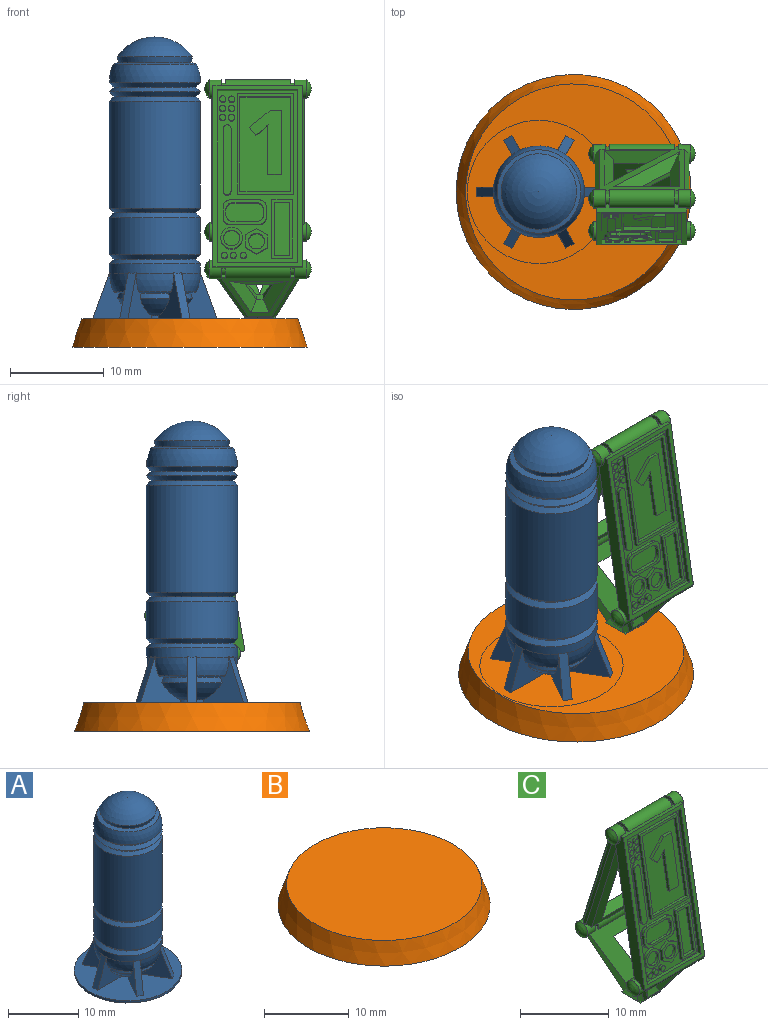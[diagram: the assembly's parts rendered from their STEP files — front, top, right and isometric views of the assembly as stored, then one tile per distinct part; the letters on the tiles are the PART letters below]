
ASSEMBLY  parts=3 mates=2
PART A: 66 faces, bbox 15.5x15.5x30.6 mm
  f0: cylinder r=4.85mm len=9.7mm, axis (0,0,-1), area 30.3mm2, adj f3,f8,f13,f18,f22,f28,f29,f48
  f1: plane 15.25x15.25mm, normal (0,0,1), area 143.6mm2, adj f2,f7,f12,f17,f26,f33,f34,f48
  f2: cylinder r=1.76mm len=0.71mm, axis (0,0,-1), area 0.3mm2, adj f1,f32,f49,f63
  f3: sphere r=4.85mm, area 7.9mm2, adj f0,f4,f60,f64
  f4: cone r=4.44mm half-angle=74deg, axis (0,0,1), area 2.1mm2, adj f3,f5,f60,f64
  f5: cone r=3.84mm half-angle=16deg, axis (0,0,-1), area 1.9mm2, adj f4,f6,f60,f64
  f6: sphere r=4.85mm, area 5.7mm2, adj f5,f7,f60,f64
  f7: cylinder r=1.76mm len=0.82mm, axis (0,0,-1), area 0.3mm2, adj f1,f6,f60,f64
  f8: sphere r=4.85mm, area 7.9mm2, adj f0,f9,f57,f61
  f9: cone r=4.44mm half-angle=74deg, axis (0,0,1), area 2.1mm2, adj f8,f10,f57,f61
  f10: cone r=3.84mm half-angle=16deg, axis (0,0,-1), area 1.9mm2, adj f9,f11,f57,f61
  f11: sphere r=4.85mm, area 5.7mm2, adj f10,f12,f57,f61
  f12: cylinder r=1.76mm len=0.71mm, axis (0,0,-1), area 0.3mm2, adj f1,f11,f57,f61
  f13: sphere r=4.85mm, area 7.9mm2, adj f0,f14,f54,f58
  f14: cone r=4.44mm half-angle=74deg, axis (0,0,1), area 2.1mm2, adj f13,f15,f54,f58
  f15: cone r=3.84mm half-angle=16deg, axis (0,0,-1), area 1.9mm2, adj f14,f16,f54,f58
  f16: sphere r=4.85mm, area 5.7mm2, adj f15,f17,f54,f58
  f17: cylinder r=1.76mm len=0.71mm, axis (0,0,-1), area 0.3mm2, adj f1,f16,f54,f58
  f18: sphere r=4.85mm, area 7.9mm2, adj f0,f19,f51,f55
  f19: cone r=4.44mm half-angle=74deg, axis (0,0,1), area 2.1mm2, adj f18,f20,f51,f55
  f20: cone r=3.84mm half-angle=16deg, axis (0,0,-1), area 1.9mm2, adj f19,f21,f51,f55
  f21: sphere r=4.85mm, area 5.7mm2, adj f20,f26,f51,f55
  f22: sphere r=4.85mm, area 7.9mm2, adj f0,f23,f48,f52
  f23: cone r=4.44mm half-angle=74deg, axis (0,0,1), area 2.1mm2, adj f22,f24,f48,f52
  f24: cone r=3.84mm half-angle=16deg, axis (0,0,-1), area 1.9mm2, adj f23,f25,f48,f52
  f25: sphere r=4.85mm, area 5.7mm2, adj f24,f33,f48,f52
  f26: cylinder r=1.76mm len=0.82mm, axis (0,0,-1), area 0.3mm2, adj f1,f21,f51,f55
  f27: cone r=4.85mm half-angle=45deg, axis (0,0,1), area 20.3mm2, adj f28,f47
  f28: cone r=4.35mm half-angle=45deg, axis (0,0,-1), area 20.3mm2, adj f0,f27
  f29: sphere r=4.85mm, area 7.9mm2, adj f0,f30,f49,f63
  f30: cone r=4.44mm half-angle=74deg, axis (0,0,1), area 2.1mm2, adj f29,f31,f49,f63
  f31: cone r=3.84mm half-angle=16deg, axis (0,0,-1), area 1.9mm2, adj f30,f32,f49,f63
  f32: sphere r=4.85mm, area 5.7mm2, adj f2,f31,f49,f63
  f33: cylinder r=1.76mm len=0.71mm, axis (0,0,-1), area 0.3mm2, adj f1,f25,f48,f52
  f34: cylinder r=7.62mm len=15.25mm, axis (0,0,-1), area 18.3mm2, adj f1,f35
  f35: plane 15.25x15.25mm, normal (0,0,-1), area 182.6mm2, adj f34
  f36: sphere r=4.85mm, area 64.8mm2, adj f37
  f37: cone r=3.84mm half-angle=16deg, axis (0,0,1), area 15.3mm2, adj f36,f38
  f38: cone r=4.44mm half-angle=74deg, axis (0,0,-1), area 16.1mm2, adj f37,f39
  f39: sphere r=4.85mm, area 59.6mm2, adj f38,f40
  f40: cone r=4.85mm half-angle=45deg, axis (0,0,1), area 20.4mm2, adj f39,f41
  f41: cone r=4.35mm half-angle=45deg, axis (0,0,-1), area 20.4mm2, adj f40,f42
  f42: cone r=4.35mm half-angle=45deg, axis (0,0,1), area 20.3mm2, adj f41,f43
  f43: cone r=4.85mm half-angle=45deg, axis (0,0,-1), area 20.3mm2, adj f42,f44
  f44: cylinder r=4.85mm len=11.39mm, axis (0,0,-1), area 346.9mm2, adj f43,f45
  f45: cone r=4.85mm half-angle=46.1deg, axis (0,0,1), area 20mm2, adj f44,f46
  f46: cone r=4.35mm half-angle=43.9deg, axis (0,0,-1), area 20.8mm2, adj f45,f47
  f47: cylinder r=4.85mm len=9.7mm, axis (0,0,-1), area 119.8mm2, adj f27,f46
  f48: plane 5.17x5.16mm, normal (0,-1,0), area 9.5mm2, adj f0,f1,f22,f23,f24,f25,f33,f50
  f49: plane 5.17x5.16mm, normal (0,1,0), area 9.5mm2, adj f0,f1,f2,f29,f30,f31,f32,f50
  f50: plane 4.96x1.83mm, normal (-0.94,0,0.34), area 5.2mm2, adj f0,f1,f48,f49
  f51: plane 5.16x4.51mm, normal (0.87,-0.5,0), area 9.5mm2, adj f0,f1,f18,f19,f20,f21,f26,f53
  f52: plane 5.16x4.51mm, normal (-0.87,0.5,0), area 9.5mm2, adj f0,f1,f22,f23,f24,f25,f33,f53
  f53: plane 4.92x2.05mm, normal (-0.47,-0.81,0.34), area 5.2mm2, adj f0,f1,f51,f52
  f54: plane 5.16x4.51mm, normal (0.87,0.5,0), area 9.5mm2, adj f0,f1,f13,f14,f15,f16,f17,f56
  f55: plane 5.16x4.51mm, normal (-0.87,-0.5,0), area 9.5mm2, adj f0,f1,f18,f19,f20,f21,f26,f56
  f56: plane 4.92x2.05mm, normal (0.47,-0.81,0.34), area 5.2mm2, adj f0,f1,f54,f55
  f57: plane 5.17x5.16mm, normal (0,1,0), area 9.5mm2, adj f0,f1,f8,f9,f10,f11,f12,f59
  f58: plane 5.17x5.16mm, normal (0,-1,0), area 9.5mm2, adj f0,f1,f13,f14,f15,f16,f17,f59
  f59: plane 4.92x1.79mm, normal (0.94,0,0.34), area 5.2mm2, adj f0,f1,f57,f58
  f60: plane 5.16x4.51mm, normal (-0.87,0.5,0), area 9.5mm2, adj f0,f1,f3,f4,f5,f6,f7,f62
  f61: plane 5.16x4.51mm, normal (0.87,-0.5,0), area 9.5mm2, adj f0,f1,f8,f9,f10,f11,f12,f62
  f62: plane 4.92x2.05mm, normal (0.47,0.81,0.34), area 5.2mm2, adj f0,f1,f60,f61
  f63: plane 5.16x4.51mm, normal (-0.87,-0.5,0), area 9.5mm2, adj f0,f1,f2,f29,f30,f31,f32,f65
  f64: plane 5.16x4.51mm, normal (0.87,0.5,0), area 9.5mm2, adj f0,f1,f3,f4,f5,f6,f7,f65
  f65: plane 4.92x2.05mm, normal (-0.47,0.81,0.34), area 5.2mm2, adj f0,f1,f63,f64
PART B: 5 faces, bbox 25x25x3 mm
  f0: plane 25x25mm, normal (0,0,-1), area 483.3mm2, adj f2,f3
  f1: plane 23x23mm, normal (0,0,1), area 415.5mm2, adj f2
  f2: cone r=12.5mm half-angle=18.4deg, axis (0,0,-1), area 238.4mm2, adj f0,f1
  f3: cylinder r=1.55mm len=3.1mm, axis (0,0,-1), area 22.4mm2, adj f0,f4
  f4: plane 3.1x3.1mm, normal (0,0,-1), area 7.5mm2, adj f3
PART C: 207 faces, bbox 11.4x10.7x25.5 mm
  f0: plane 0.4x0.15mm, normal (0,0,1), area 0.1mm2, adj f2,f25,f26,f30
  f1: plane 7.81x4.18mm, normal (0,-0.84,-0.54), area 8.5mm2, adj f4,f5,f9,f10,f11,f16,f17,f18
  f2: plane 9.66x5.27mm, normal (0,0.73,0.68), area 30.6mm2, adj f0,f3,f6,f7,f8,f12,f13,f14
  f3: plane 5.37x5.03mm, normal (-0.82,0,-0.57), area 10.8mm2, adj f2,f5,f6,f35
  f4: plane 0.4x0.25mm, normal (0,-0.88,0.48), area 0.1mm2, adj f1,f36,f37,f38
  f5: plane 4.35x3.29mm, normal (-0.51,-0.52,-0.69), area 3.6mm2, adj f1,f3,f11,f20,f22,f35,f36
  f6: plane 3.1x3.04mm, normal (0,0,-1), area 9.4mm2, adj f2,f3,f8,f20,f21,f22
  f7: plane 0.4x0.15mm, normal (0,0,1), area 0.1mm2, adj f2,f27,f28,f29
  f8: plane 5.35x5.03mm, normal (0.85,0,-0.52), area 10.3mm2, adj f2,f6,f10,f34
  f9: plane 0.4x0.25mm, normal (0,-0.88,0.48), area 0.1mm2, adj f1,f40,f41,f42
  f10: plane 4.32x3.22mm, normal (0.53,-0.53,-0.66), area 3.6mm2, adj f1,f8,f11,f20,f21,f34
  f11: plane 2.64x0.23mm, normal (0,-0.48,-0.88), area 0.7mm2, adj f1,f5,f10,f20
  f12: plane 0.78x0.73mm, normal (0,-0.54,0.84), area 0.7mm2, adj f2,f13,f14,f19
  f13: plane 1.96x1.84mm, normal (0.86,-0.27,0.42), area 1.7mm2, adj f2,f12,f15,f17
  f14: plane 1.96x1.84mm, normal (-0.89,-0.25,0.38), area 1.7mm2, adj f2,f12,f15,f18
  f15: plane 2.89x0.48mm, normal (0,0.54,-0.84), area 1.6mm2, adj f2,f13,f14,f16
  f16: plane 6.27x1.38mm, normal (0,-0.21,-0.98), area 6.5mm2, adj f1,f15,f17,f18
  f17: plane 3.34x2.89mm, normal (0.61,-0.79,-0.08), area 4.9mm2, adj f1,f13,f16,f19
  f18: plane 3.34x2.64mm, normal (-0.63,-0.77,-0.11), area 4.7mm2, adj f1,f14,f16,f19
  f19: plane 1.92x1.38mm, normal (0,-0.98,0.21), area 1.9mm2, adj f1,f12,f17,f18
  f20: plane 3.33x0.33mm, normal (0,-0.89,0.46), area 0.5mm2, adj f5,f6,f10,f11,f21,f22
  f21: plane 0.47x0.33mm, normal (0.95,0,-0.33), area 0.1mm2, adj f6,f10,f20
  f22: plane 0.45x0.31mm, normal (-0.93,0,-0.37), area 0.1mm2, adj f5,f6,f20
  f23: cylinder r=1mm len=6.97mm, axis (1,0,0), area 11.4mm2, adj f1,f38,f40,f115
  f24: plane 1.1x0.37mm, normal (0,0.58,-0.82), area 0.4mm2, adj f2,f48,f49,f55
  f25: cylinder r=0.6mm len=0.59mm, axis (1,0,0), area 0.3mm2, adj f0,f26,f30,f116
  f26: plane 1.22x0.9mm, normal (-1,0,0), area 0.5mm2, adj f0,f2,f25,f39,f116
  f27: plane 1.22x0.9mm, normal (1,0,0), area 0.5mm2, adj f2,f7,f28,f39,f116
  f28: cylinder r=0.6mm len=0.59mm, axis (1,0,0), area 0.3mm2, adj f7,f27,f29,f116
  f29: plane 1.22x0.9mm, normal (-1,0,0), area 0.5mm2, adj f2,f7,f28,f34,f116
  f30: plane 1.22x0.9mm, normal (1,0,0), area 0.5mm2, adj f0,f2,f25,f35,f116
  f31: plane 8.42x4.24mm, normal (-0.93,0,-0.37), area 12.3mm2, adj f2,f33,f50,f70
  f32: plane 8.41x4.23mm, normal (0.95,0,-0.33), area 12mm2, adj f2,f33,f49,f67
  f33: plane 9.72x7.18mm, normal (0,-0.89,0.46), area 45.6mm2, adj f2,f31,f32,f45,f47,f52,f53,f54
  f34: cylinder r=1mm len=2mm, axis (1,0,0), area 6mm2, adj f1,f2,f8,f10,f29,f42,f43,f112
  f35: cylinder r=1mm len=2mm, axis (1,0,0), area 6.1mm2, adj f2,f3,f5,f30,f36,f44,f114,f115
  f36: plane 1.17x0.95mm, normal (1,0,0), area 0.5mm2, adj f1,f4,f5,f35,f37,f115
  f37: cylinder r=0.6mm len=0.7mm, axis (1,0,0), area 0.4mm2, adj f4,f36,f38,f115
  f38: plane 1.17x0.93mm, normal (-1,0,0), area 0.5mm2, adj f1,f4,f23,f37,f115
  f39: cylinder r=1mm len=6.97mm, axis (1,0,0), area 11.4mm2, adj f2,f26,f27,f116
  f40: plane 1.17x0.93mm, normal (1,0,0), area 0.5mm2, adj f1,f9,f23,f41,f115
  f41: cylinder r=0.6mm len=0.7mm, axis (1,0,0), area 0.4mm2, adj f9,f40,f42,f115
  f42: plane 1.17x0.93mm, normal (-1,0,0), area 0.5mm2, adj f1,f9,f34,f41,f115
  f43: revolved ~2x2mm, area 3.8mm2, adj f34
  f44: revolved ~2x2mm, area 3.8mm2, adj f35
  f45: plane 0.4x0.16mm, normal (0,0,1), area 0.1mm2, adj f33,f58,f60,f61
  f46: plane 8.03x0.37mm, normal (0,0.82,0.58), area 0.6mm2, adj f48,f49,f50,f65,f66,f67,f70,f71
  f47: plane 0.4x0.16mm, normal (0,0,1), area 0.1mm2, adj f33,f59,f63,f64
  f48: plane 7.94x7.85mm, normal (0,0.94,-0.33), area 12.2mm2, adj f24,f46,f49,f50,f51,f55,f56,f57
  f49: plane 8.15x3.45mm, normal (0.63,0.63,-0.44), area 8.3mm2, adj f2,f24,f32,f46,f48,f67
  f50: plane 8.15x3.77mm, normal (-0.62,0.63,-0.47), area 8.4mm2, adj f2,f31,f46,f48,f51,f70
  f51: plane 1.12x0.37mm, normal (0,0.58,-0.82), area 0.4mm2, adj f2,f48,f50,f57
  f52: plane 5.25x3.14mm, normal (-0.95,0.1,0.29), area 6mm2, adj f33,f53,f54,f55
  f53: plane 5.25x3.14mm, normal (0.94,0.12,0.33), area 6.1mm2, adj f33,f52,f54,f57
  f54: plane 3.71x0.67mm, normal (0,-0.33,-0.94), area 2.7mm2, adj f33,f52,f53,f56
  f55: plane 7.64x3.11mm, normal (-0.67,0.74,-0.03), area 10.5mm2, adj f2,f24,f48,f52,f56,f57
  f56: plane 6.53x1.28mm, normal (0,0.43,-0.9), area 7.2mm2, adj f48,f54,f55,f57
  f57: plane 7.64x3.46mm, normal (0.66,0.75,0), area 10.7mm2, adj f2,f48,f51,f53,f55,f56
  f58: cylinder r=0.6mm len=0.4mm, axis (1,0,0), area 0.1mm2, adj f45,f60,f61,f79
  f59: cylinder r=0.6mm len=0.4mm, axis (1,0,0), area 0.1mm2, adj f47,f63,f64,f87
  f60: plane 0.78x0.42mm, normal (1,0,0), area 0.2mm2, adj f33,f45,f58,f70,f77,f79
  f61: plane 0.78x0.42mm, normal (-1,0,0), area 0.2mm2, adj f33,f45,f58,f62,f77,f79
  f62: cylinder r=1mm len=6.97mm, axis (1,0,0), area 5.6mm2, adj f33,f61,f63,f77
  f63: plane 0.78x0.42mm, normal (1,0,0), area 0.2mm2, adj f33,f47,f59,f62,f77,f87
  f64: plane 0.78x0.42mm, normal (-1,0,0), area 0.2mm2, adj f33,f47,f59,f67,f77,f87
  f65: cylinder r=0.6mm len=0.57mm, axis (1,0,0), area 0.3mm2, adj f46,f71,f72,f78
  f66: cylinder r=0.6mm len=0.57mm, axis (1,0,0), area 0.3mm2, adj f46,f74,f75,f83
  f67: cylinder r=1mm len=2mm, axis (1,0,0), area 5.6mm2, adj f32,f33,f46,f49,f64,f68,f75,f76
  f68: revolved ~2x2mm, area 3.8mm2, adj f67
  f69: revolved ~2x2mm, area 3.8mm2, adj f70
  f70: cylinder r=1mm len=2mm, axis (1,0,0), area 5.7mm2, adj f31,f33,f46,f50,f60,f69,f71,f76
  f71: plane 1.78x0.82mm, normal (1,0,0), area 0.6mm2, adj f46,f65,f70,f76,f78
  f72: plane 1.78x0.82mm, normal (-1,0,0), area 0.6mm2, adj f46,f65,f73,f76,f78
  f73: cylinder r=1mm len=6.97mm, axis (1,0,0), area 15.3mm2, adj f46,f72,f74,f76
  f74: plane 1.78x0.82mm, normal (1,0,0), area 0.6mm2, adj f46,f66,f73,f76,f83
  f75: plane 1.78x0.82mm, normal (-1,0,0), area 0.6mm2, adj f46,f66,f67,f76,f83
  f76: plane 15.2x8.97mm, normal (0,0.95,0.3), area 44.3mm2, adj f67,f70,f71,f72,f73,f74,f75,f78
  f77: plane 13.5x8.97mm, normal (0,-0.96,-0.3), area 83.3mm2, adj f60,f61,f62,f63,f64,f67,f70,f79
  f78: plane 0.4x0.17mm, normal (0,0,-1), area 0.1mm2, adj f65,f71,f72,f76
  f79: plane 0.4x0.29mm, normal (0,-0.59,-0.8), area 0.1mm2, adj f58,f60,f61,f77
  f80: plane 0.4x0.24mm, normal (0,0,1), area 0.1mm2, adj f76,f104,f105,f106
  f81: plane 13.78x4.55mm, normal (-0.71,-0.68,-0.21), area 10mm2, adj f70,f77,f84,f103,f116
  f82: plane 0.4x0.24mm, normal (0,0,1), area 0.1mm2, adj f76,f108,f109,f110
  f83: plane 0.4x0.17mm, normal (0,0,-1), area 0.1mm2, adj f66,f74,f75,f76
  f84: plane 13.52x4.58mm, normal (-1,0,0), area 6.3mm2, adj f70,f81,f88,f103
  f85: plane 13.52x4.58mm, normal (1,0,0), area 6.3mm2, adj f67,f86,f89,f100
  f86: plane 13.78x4.55mm, normal (0.71,-0.68,-0.21), area 10mm2, adj f67,f77,f85,f100,f116
  f87: plane 0.4x0.29mm, normal (0,-0.59,-0.8), area 0.1mm2, adj f59,f63,f64,f77
  f88: plane 14.01x4.74mm, normal (-0.71,0.68,0.21), area 10.1mm2, adj f70,f76,f84,f103
  f89: plane 14.01x4.74mm, normal (0.71,0.68,0.21), area 10.1mm2, adj f67,f76,f85,f100
  f90: plane 7.05x1.39mm, normal (0,-0.3,0.95), area 8.2mm2, adj f76,f77,f91,f92,f96,f97
  f91: plane 8.45x3.02mm, normal (1,0,0), area 3.9mm2, adj f77,f90,f92,f97
  f92: plane 8.45x4.9mm, normal (-0.87,0.15,-0.47), area 4.5mm2, adj f77,f90,f91,f96
  f93: plane 7.05x1.37mm, normal (0,0.3,-0.95), area 8.1mm2, adj f76,f77,f94,f95,f98,f99
  f94: plane 8.45x3.01mm, normal (-1,0,0), area 3.9mm2, adj f77,f93,f95,f99
  f95: plane 8.45x4.9mm, normal (0.87,-0.15,0.47), area 4.4mm2, adj f77,f93,f94,f98
  f96: plane 12.25x7.05mm, normal (-0.62,0.78,-0.12), area 17.2mm2, adj f76,f90,f92,f97
  f97: plane 12.25x3.73mm, normal (0.71,0.68,0.21), area 15mm2, adj f76,f90,f91,f96
  f98: plane 11.95x7.05mm, normal (0.62,0.57,0.54), area 17.2mm2, adj f76,f93,f95,f99
  f99: plane 11.95x4.68mm, normal (-0.71,0.68,0.21), area 15mm2, adj f76,f93,f94,f98
  f100: cylinder r=1mm len=2mm, axis (1,0,0), area 5.4mm2, adj f76,f85,f86,f89,f101,f110,f112,f113
  f101: revolved ~2x2mm, area 3.8mm2, adj f100
  f102: revolved ~2x2mm, area 3.8mm2, adj f103
  f103: cylinder r=1mm len=2mm, axis (1,0,0), area 5.3mm2, adj f76,f81,f84,f88,f102,f104,f113,f114
  f104: plane 1.95x1.33mm, normal (1,0,0), area 0.9mm2, adj f76,f80,f103,f105,f113
  f105: cylinder r=0.6mm len=1.15mm, axis (1,0,0), area 0.7mm2, adj f80,f104,f106,f113
  f106: plane 1.95x1.33mm, normal (-1,0,0), area 0.9mm2, adj f76,f80,f105,f107,f113
  f107: cylinder r=1mm len=6.97mm, axis (1,0,0), area 22.1mm2, adj f76,f106,f108,f113
  f108: plane 1.95x1.33mm, normal (1,0,0), area 0.9mm2, adj f76,f82,f107,f109,f113
  f109: cylinder r=0.6mm len=1.15mm, axis (1,0,0), area 0.7mm2, adj f82,f108,f110,f113
  f110: plane 1.95x1.33mm, normal (-1,0,0), area 0.9mm2, adj f76,f82,f100,f109,f113
  f111: plane 18.35x8.54mm, normal (0,-0.98,0.17), area 49.9mm2, adj f117,f118,f119,f120,f122,f123,f124,f129
  f112: plane 19.42x4.69mm, normal (1,0,0), area 27.7mm2, adj f34,f100,f113,f115,f116,f121
  f113: plane 9.54x0.9mm, normal (0,0.17,0.98), area 5.2mm2, adj f100,f103,f104,f105,f106,f107,f108,f109
  f114: plane 19.42x4.69mm, normal (-1,0,0), area 27.7mm2, adj f35,f103,f113,f115,f116,f121
  f115: plane 9.54x0.89mm, normal (0,-0.17,-0.98), area 5.1mm2, adj f23,f34,f35,f36,f37,f38,f40,f41
  f116: plane 17.63x9.54mm, normal (0,0.98,-0.17), area 163.9mm2, adj f25,f26,f27,f28,f29,f30,f34,f35
  f117: plane 18.44x3.73mm, normal (1,0,0), area 9.3mm2, adj f111,f118,f120,f121
  f118: plane 8.54x0.49mm, normal (0,-0.17,-0.98), area 4.3mm2, adj f111,f117,f119,f121
  f119: plane 18.44x3.73mm, normal (-1,0,0), area 9.3mm2, adj f111,f118,f120,f121
  f120: plane 8.54x0.49mm, normal (0,0.17,0.98), area 4.3mm2, adj f111,f117,f119,f121
  f121: plane 19.33x9.54mm, normal (0,-0.98,0.17), area 28.2mm2, adj f112,f113,f114,f115,f117,f118,f119,f120
  f122: plane 6x0.39mm, normal (0,0.17,0.98), area 2.4mm2, adj f111,f123,f129,f130
  f123: plane 10.76x2.28mm, normal (-1,0,0), area 4.3mm2, adj f111,f122,f124,f130
  f124: plane 6x0.39mm, normal (0,-0.17,-0.98), area 2.4mm2, adj f111,f123,f129,f130
  f125: plane 5.4x0.39mm, normal (0,-0.17,-0.98), area 2.2mm2, adj f126,f128,f130,f131
  f126: plane 10.17x2.17mm, normal (-1,0,0), area 4.1mm2, adj f125,f127,f130,f131
  f127: plane 5.4x0.39mm, normal (0,0.17,0.98), area 2.2mm2, adj f126,f128,f130,f131
  f128: plane 10.17x2.17mm, normal (1,0,0), area 4.1mm2, adj f125,f127,f130,f131
  f129: plane 10.76x2.28mm, normal (1,0,0), area 4.3mm2, adj f111,f122,f124,f130
  f130: plane 10.69x6mm, normal (0,-0.98,0.17), area 9.8mm2, adj f122,f123,f124,f125,f126,f127,f128,f129
  f131: plane 10.1x5.4mm, normal (0,-0.98,0.17), area 43.2mm2, adj f125,f126,f127,f128,f196,f197,f198,f199
  f132: cylinder r=0.32mm len=0.7mm, axis (0,0.98,-0.17), area 0.8mm2, adj f111,f133
  f133: plane 0.65x0.64mm, normal (0,-0.98,0.17), area 0.3mm2, adj f132
  f134: cylinder r=0.32mm len=0.7mm, axis (0,0.98,-0.17), area 0.8mm2, adj f111,f135
  f135: plane 0.65x0.64mm, normal (0,-0.98,0.17), area 0.3mm2, adj f134
  f136: cylinder r=0.32mm len=0.7mm, axis (0,0.98,-0.17), area 0.8mm2, adj f111,f137
  f137: plane 0.65x0.64mm, normal (0,-0.98,0.17), area 0.3mm2, adj f136
  f138: cylinder r=0.32mm len=0.7mm, axis (0,0.98,-0.17), area 0.8mm2, adj f111,f139
  f139: plane 0.65x0.64mm, normal (0,-0.98,0.17), area 0.3mm2, adj f138
  f140: cylinder r=0.32mm len=0.7mm, axis (0,0.98,-0.17), area 0.8mm2, adj f111,f141
  f141: plane 0.65x0.64mm, normal (0,-0.98,0.17), area 0.3mm2, adj f140
  f142: cylinder r=0.32mm len=0.7mm, axis (0,0.98,-0.17), area 0.8mm2, adj f111,f143
  f143: plane 0.65x0.64mm, normal (0,-0.98,0.17), area 0.3mm2, adj f142
  f144: cylinder r=0.42mm len=0.85mm, axis (0,0.98,-0.17), area 0.5mm2, adj f111,f145,f147,f148
  f145: plane 6.67x1.56mm, normal (-1,0,0), area 2.7mm2, adj f111,f144,f146,f148
  f146: cylinder r=0.42mm len=0.85mm, axis (0,0.98,-0.17), area 0.5mm2, adj f111,f145,f147,f148
  f147: plane 6.67x1.56mm, normal (1,0,0), area 2.7mm2, adj f111,f144,f146,f148
  f148: plane 7.44x1.31mm, normal (0,-0.98,0.17), area 6.3mm2, adj f144,f145,f146,f147
  f149: plane 3.1x0.39mm, normal (0,0.17,0.98), area 1.2mm2, adj f111,f150,f164,f165
  f150: cylinder r=0.75mm len=0.81mm, axis (0,0.98,-0.17), area 0.5mm2, adj f111,f149,f151,f165
  f151: plane 1.19x0.59mm, normal (-1,0,0), area 0.5mm2, adj f111,f150,f152,f165
  f152: cylinder r=0.75mm len=0.81mm, axis (0,0.98,-0.17), area 0.5mm2, adj f111,f151,f153,f165
  f153: plane 3.1x0.39mm, normal (0,-0.17,-0.98), area 1.2mm2, adj f111,f152,f154,f165
  f154: cylinder r=0.75mm len=0.81mm, axis (0,0.98,-0.17), area 0.5mm2, adj f111,f153,f155,f165
  f155: plane 1.19x0.59mm, normal (1,0,0), area 0.5mm2, adj f111,f154,f164,f165
  f156: cylinder r=0.75mm len=0.81mm, axis (0,0.98,-0.17), area 0.5mm2, adj f157,f163,f165,f166
  f157: plane 2.5x0.39mm, normal (0,-0.17,-0.98), area 1mm2, adj f156,f158,f165,f166
  f158: cylinder r=0.75mm len=0.81mm, axis (0,0.98,-0.17), area 0.5mm2, adj f157,f159,f165,f166
  f159: plane 0.6x0.49mm, normal (-1,0,0), area 0.2mm2, adj f158,f160,f165,f166
  f160: cylinder r=0.75mm len=0.81mm, axis (0,0.98,-0.17), area 0.5mm2, adj f159,f161,f165,f166
  f161: plane 2.5x0.39mm, normal (0,0.17,0.98), area 1mm2, adj f160,f162,f165,f166
  f162: cylinder r=0.75mm len=0.81mm, axis (0,0.98,-0.17), area 0.5mm2, adj f161,f163,f165,f166
  f163: plane 0.6x0.49mm, normal (1,0,0), area 0.2mm2, adj f156,f162,f165,f166
  f164: cylinder r=0.75mm len=0.81mm, axis (0,0.98,-0.17), area 0.5mm2, adj f111,f149,f155,f165
  f165: plane 4.6x2.6mm, normal (0,-0.98,0.17), area 4mm2, adj f149,f150,f151,f152,f153,f154,f155,f156
  f166: plane 4x2.01mm, normal (0,-0.98,0.17), area 7.7mm2, adj f156,f157,f158,f159,f160,f161,f162,f163
  f167: plane 2.23x0.39mm, normal (0,0.17,0.98), area 0.9mm2, adj f111,f168,f174,f175
  f168: plane 6.32x1.5mm, normal (-1,0,0), area 2.5mm2, adj f111,f167,f169,f175
  f169: plane 2.23x0.39mm, normal (0,-0.17,-0.98), area 0.9mm2, adj f111,f168,f174,f175
  f170: plane 1.63x0.39mm, normal (0,-0.17,-0.98), area 0.7mm2, adj f171,f173,f175,f176
  f171: plane 5.73x1.39mm, normal (-1,0,0), area 2.3mm2, adj f170,f172,f175,f176
  f172: plane 1.63x0.39mm, normal (0,0.17,0.98), area 0.7mm2, adj f171,f173,f175,f176
  f173: plane 5.73x1.39mm, normal (1,0,0), area 2.3mm2, adj f170,f172,f175,f176
  f174: plane 6.32x1.5mm, normal (1,0,0), area 2.5mm2, adj f111,f167,f169,f175
  f175: plane 6.25x2.23mm, normal (0,-0.98,0.17), area 4.8mm2, adj f167,f168,f169,f170,f171,f172,f173,f174
  f176: plane 5.66x1.63mm, normal (0,-0.98,0.17), area 9.4mm2, adj f170,f171,f172,f173
  f177: cylinder r=0.85mm len=1.75mm, axis (0,0.98,-0.17), area 2.1mm2, adj f179,f180
  f178: cylinder r=1.15mm len=2.34mm, axis (0,0.98,-0.17), area 2.9mm2, adj f111,f179
  f179: plane 2.31x2.27mm, normal (0,-0.98,0.17), area 1.9mm2, adj f177,f178
  f180: plane 1.71x1.68mm, normal (0,-0.98,0.17), area 2.3mm2, adj f177
  f181: plane 1.42x0.63mm, normal (-1,0,0.01), area 0.5mm2, adj f111,f182,f187,f188
  f182: plane 1.18x0.75mm, normal (-0.51,-0.15,-0.85), area 0.5mm2, adj f111,f181,f183,f188
  f183: plane 1.19x0.73mm, normal (0.49,-0.15,-0.86), area 0.5mm2, adj f111,f182,f184,f188
  f184: plane 1.42x0.63mm, normal (1,0,-0.01), area 0.5mm2, adj f111,f183,f185,f188
  f185: plane 1.18x0.75mm, normal (0.51,0.15,0.85), area 0.5mm2, adj f111,f184,f187,f188
  f186: cylinder r=0.85mm len=1.74mm, axis (0,0.98,-0.17), area 2.1mm2, adj f188,f189
  f187: plane 1.19x0.73mm, normal (-0.49,0.15,0.86), area 0.5mm2, adj f111,f181,f185,f188
  f188: plane 2.69x2.38mm, normal (0,-0.98,0.17), area 2.6mm2, adj f181,f182,f183,f184,f185,f186,f187
  f189: plane 1.7x1.68mm, normal (0,-0.98,0.17), area 2.3mm2, adj f186
  f190: cylinder r=0.32mm len=0.7mm, axis (0,0.98,-0.17), area 0.8mm2, adj f111,f191
  f191: plane 0.65x0.64mm, normal (0,-0.98,0.17), area 0.3mm2, adj f190
  f192: cylinder r=0.32mm len=0.7mm, axis (0,0.98,-0.17), area 0.8mm2, adj f111,f193
  f193: plane 0.65x0.64mm, normal (0,-0.98,0.17), area 0.3mm2, adj f192
  f194: cylinder r=0.32mm len=0.7mm, axis (0,0.98,-0.17), area 0.8mm2, adj f111,f195
  f195: plane 0.65x0.64mm, normal (0,-0.98,0.17), area 0.3mm2, adj f194
  f196: plane 1.45x0.39mm, normal (0,-0.17,-0.98), area 0.6mm2, adj f131,f197,f205,f206
  f197: plane 6.84x1.59mm, normal (1,0,0), area 2.8mm2, adj f131,f196,f198,f206
  f198: plane 1.2x0.39mm, normal (0,0.17,0.98), area 0.5mm2, adj f131,f197,f199,f206
  f199: plane 2.22x1.81mm, normal (-0.62,0.14,0.77), area 1.1mm2, adj f131,f198,f200,f206
  f200: plane 0.93x0.7mm, normal (-0.78,-0.11,-0.62), area 0.4mm2, adj f131,f199,f201,f206
  f201: plane 0.79x0.7mm, normal (0.63,-0.14,-0.77), area 0.4mm2, adj f131,f200,f202,f206
  f202: extruded ~0.54x0.5mm, area 0.3mm2, adj f131,f201,f203,f206
  f203: plane 0.77x0.52mm, normal (-1,0.01,0.03), area 0.3mm2, adj f131,f202,f204,f206
  f204: plane 0.71x0.51mm, normal (-1,0,0.02), area 0.3mm2, adj f131,f203,f205,f206
  f205: plane 3.99x1.09mm, normal (-1,0,0), area 1.6mm2, adj f131,f196,f204,f206
  f206: plane 6.77x3.41mm, normal (0,-0.98,0.17), area 12.2mm2, adj f196,f197,f198,f199,f200,f201,f202,f203
PLACE A t=(-0.7,0,0)mm
PLACE B at identity
PLACE C t=(1.27,1.62,0)mm
MATE fastened C.f6 <-> B.f1  axis (0,0,-1) through (7.5,0,3)mm
MATE fastened A.f0 <-> B.f1  axis (0,0,1) through (-3.7,0,3)mm
